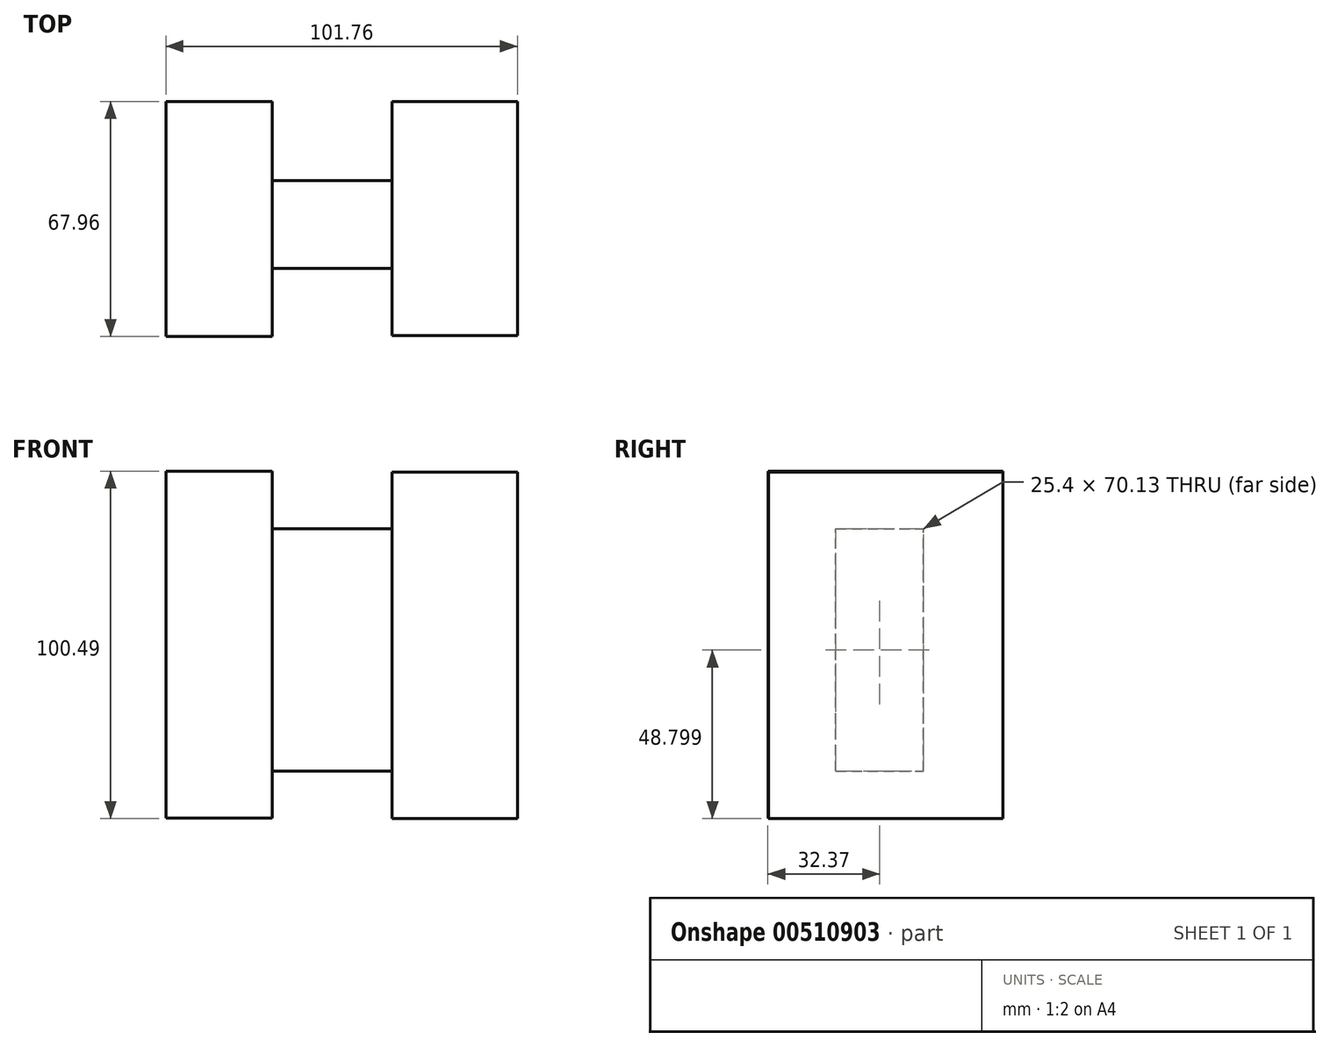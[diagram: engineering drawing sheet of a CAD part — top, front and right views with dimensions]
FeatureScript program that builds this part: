
annotation { "Feature Type Name" : "Feature", "Feature Type Description" : "" }
export const myFeature = defineFeature(function(context is Context, id is Id, definition is map)
    precondition{}
    {
        {
            var Q0;
            Q0=qCreatedBy(makeId("Front.planeOp"),FACE);
            var sketch = newSketch(context, id + "F0", { "sketchPlane" : qUnion([Q0])});
            skLineSegment(sketch, "E0.bottom", {"start": v(-82.66, 41.7) * mm, "end": v(97.12, 41.7) * mm});
            skLineSegment(sketch, "E0.top", {"start": v(-82.66, -45.07) * mm, "end": v(97.12, -45.07) * mm});
            skLineSegment(sketch, "E0.left", {"start": v(-82.66, 41.7) * mm, "end": v(-82.66, -45.07) * mm});
            skLineSegment(sketch, "E0.right", {"start": v(97.12, 41.7) * mm, "end": v(97.12, -45.07) * mm});
            skLineSegment(sketch, "E1", {"start": v(-34.7, 39.76) * mm, "end": v(-34.7, 25.06) * mm});
            skLineSegment(sketch, "E2", {"start": v(-34.7, 25.06) * mm, "end": v(36.15, 25.06) * mm});
            skLineSegment(sketch, "E3", {"start": v(36.15, 25.06) * mm, "end": v(36.15, 41.7) * mm});
            skLineSegment(sketch, "E4", {"start": v(36.15, 25.06) * mm, "end": v(36.15, -45.07) * mm});
            skLineSegment(sketch, "E5", {"start": v(-34.7, 25.06) * mm, "end": v(-34.7, -45.07) * mm});
            skSolve(sketch);
        }
        {
            var Q0;
            Q0=makeQuery(id+"F0.imprint","IMPRINT",FACE,{"disambiguationData":[TD([[makeQuery(id+"F0.imprint","IMPRINT",EDGE,{"derivedFrom":sQuery(id+"F0.wireOp",EDGE,"E2")}),-1.0]])]});
            extrude(context, id + "F1", {"entities" : qUnion([Q0]), "depth" : 25.4 * mm});
        }
        {
            var Q0;
            Q0=qCreatedBy(makeId("Right.planeOp"),FACE);
            var sketch = newSketch(context, id + "F2", { "sketchPlane" : qUnion([Q0])});
            skLineSegment(sketch, "E6.bottom", {"start": v(-44.82, 41.45) * mm, "end": v(22.9, 41.45) * mm});
            skLineSegment(sketch, "E6.top", {"start": v(-44.82, -58.8) * mm, "end": v(22.9, -58.8) * mm});
            skLineSegment(sketch, "E6.left", {"start": v(-44.82, 41.45) * mm, "end": v(-44.82, -58.8) * mm});
            skLineSegment(sketch, "E6.right", {"start": v(22.9, 41.45) * mm, "end": v(22.9, -58.8) * mm});
            skSolve(sketch);
        }
        {
            var Q0;
            Q0 = qSketchRegion(id + "F2", true);
            extrude(context, id + "F3", {"entities" : qUnion([Q0]), "operationType" : NewBodyOperationType.ADD, "depth" : 36.32 * mm});
        }
        {
            var Q0;
            Q0=makeQuery(id+"F1.opExtrude","SWEPT_FACE",FACE,{"disambiguationData":[OSD([sQuery(id+"F0.wireOp",EDGE,"E5")])]});
            var sketch = newSketch(context, id + "F4", { "sketchPlane" : qUnion([Q0])});
            skLineSegment(sketch, "E7.bottom", {"start": v(-22.9, 41.7) * mm, "end": v(45.07, 41.7) * mm});
            skLineSegment(sketch, "E7.top", {"start": v(-22.9, -58.56) * mm, "end": v(45.07, -58.56) * mm});
            skLineSegment(sketch, "E7.left", {"start": v(-22.9, 41.7) * mm, "end": v(-22.9, -58.56) * mm});
            skLineSegment(sketch, "E7.right", {"start": v(45.07, 41.7) * mm, "end": v(45.07, -58.56) * mm});
            skSolve(sketch);
        }
        {
            var Q0;
            Q0 = qSketchRegion(id + "F4", true);
            extrude(context, id + "F5", {"entities" : qUnion([Q0]), "operationType" : NewBodyOperationType.ADD, "depth" : 30.73 * mm});
        }
    });
